# Revit family: PR636
name_source: partatom
category: Mechanical Equipment
revit_build: Autodesk Revit 2018 (Build: 20170223_1515(x64)
units: mm (PartAtom-declared; Revit-internal decimal feet)

## family parameters
Always vertical = Yes
Cut with Voids When Loaded = No
OmniClass Number = 23.75.00.00
OmniClass Title = Climate Control (HVAC)
Part Type = Normal
Room Calculation Point = No
Round Connector Dimension = Use Diameter
Shared = No
Work Plane-Based = No

## types (1)
- ISOLAMIN PR636 flashing
    Edition = 1.0 (2018)
    Manufacturer = ISOLAMIN AB
    Material = Galvanized Steel
    Model = PR636
    Profile Length = 1180 mm  [stored 3.87139 ft]
    Thickness = 0.7 mm (Different thicknesses are available on request) 
0.7 mm (Different thicknesses are available on request) 
0.7 mm (Different thicknesses are available on request)
    URL = http://www.isolamin.se

note: [stored X ft] marks values corroborated as IEEE doubles in the binary element streams (Revit-internal decimal feet)

## geometry (parser evidence)
native form markers: Sweep x2
no freeform markers — native parametric forms only
